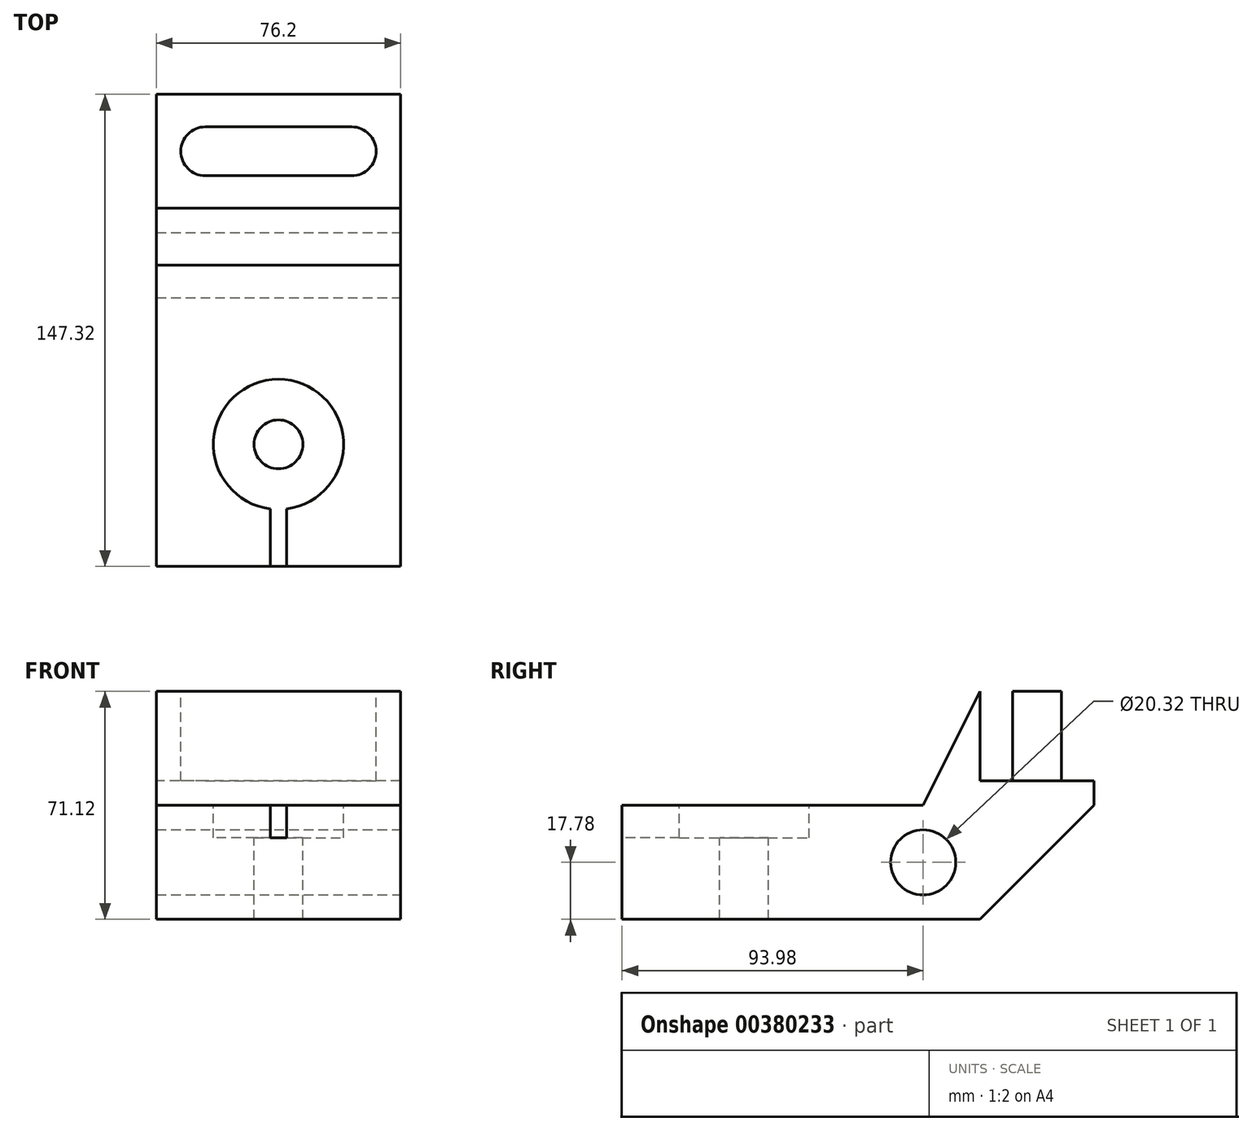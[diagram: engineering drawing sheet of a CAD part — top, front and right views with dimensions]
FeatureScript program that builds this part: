
annotation { "Feature Type Name" : "Feature", "Feature Type Description" : "" }
export const myFeature = defineFeature(function(context is Context, id is Id, definition is map)
    precondition{}
    {
        {
            var Q0;
            Q0=qCreatedBy(makeId("Right.planeOp"),FACE);
            var sketch = newSketch(context, id + "F0", { "sketchPlane" : qUnion([Q0])});
            skLineSegment(sketch, "E0.bottom", {"start": v(0, 0) * mm, "end": v(111.76, 0) * mm});
            skLineSegment(sketch, "E0.top", {"start": v(0, 35.56) * mm, "end": v(93.98, 35.56) * mm});
            skLineSegment(sketch, "E0.left", {"start": v(0, 0) * mm, "end": v(0, 35.56) * mm});
            skPoint(sketch, "E1", {"position": v(111.76, 0) * mm});
            skLineSegment(sketch, "E2", {"start": v(147.32, 35.56) * mm, "end": v(111.76, 0) * mm});
            skPoint(sketch, "E3", {"position": v(93.98, 35.56) * mm});
            skLineSegment(sketch, "E4", {"start": v(147.32, 35.56) * mm, "end": v(147.32, 71.12) * mm});
            skLineSegment(sketch, "E5", {"start": v(147.32, 71.12) * mm, "end": v(111.76, 71.12) * mm});
            skLineSegment(sketch, "E6", {"start": v(111.76, 71.12) * mm, "end": v(93.98, 35.56) * mm});
            skSolve(sketch);
        }
        {
            var Q0;
            Q0 = qSketchRegion(id + "F0", true);
            extrude(context, id + "F1", {"entities" : qUnion([Q0]), "depth" : 76.2 * mm});
        }
        {
            var Q0;
            Q0=makeQuery(id+"F1.opExtrude","CAP_FACE",FACE,{"disambiguationData":[OSD([sQuery(id+"F0.wireOp",EDGE,"E0.bottom"),sQuery(id+"F0.wireOp",EDGE,"E0.top"),sQuery(id+"F0.wireOp",EDGE,"E0.left"),sQuery(id+"F0.wireOp",EDGE,"E2"),sQuery(id+"F0.wireOp",EDGE,"E4"),sQuery(id+"F0.wireOp",EDGE,"E5"),sQuery(id+"F0.wireOp",EDGE,"E6")])],"isStart":false});
            var sketch = newSketch(context, id + "F2", { "sketchPlane" : qUnion([Q0])});
            skPoint(sketch, "E7", {"position": v(93.98, 17.78) * mm});
            skCircle(sketch, "E8", {"center": v(93.98, 17.78) * mm, "radius": 10.16 * mm});
            skSolve(sketch);
        }
        {
            var Q0;
            Q0 = qSketchRegion(id + "F2", true);
            var Q1;
            Q1=makeQuery(id+"F1.opExtrude","CAP_FACE",FACE,{"disambiguationData":[OSD([sQuery(id+"F0.wireOp",EDGE,"E0.bottom"),sQuery(id+"F0.wireOp",EDGE,"E0.top"),sQuery(id+"F0.wireOp",EDGE,"E0.left"),sQuery(id+"F0.wireOp",EDGE,"E2"),sQuery(id+"F0.wireOp",EDGE,"E4"),sQuery(id+"F0.wireOp",EDGE,"E5"),sQuery(id+"F0.wireOp",EDGE,"E6")])],"isStart":true});
            extrude(context, id + "F3", {"entities" : qUnion([Q0]), "operationType" : NewBodyOperationType.REMOVE, "endBound" : BoundingType.UP_TO_SURFACE, "oppositeDirection" : true, "endBoundEntityFace" : qUnion([Q1]), "depth" : 25.4 * mm});
        }
        {
            var Q0;
            Q0=makeQuery(id+"F1.opExtrude","SWEPT_FACE",FACE,{"disambiguationData":[OSD([sQuery(id+"F0.wireOp",EDGE,"E5")])]});
            var sketch = newSketch(context, id + "F4", { "sketchPlane" : qUnion([Q0])});
            skPoint(sketch, "E9.orphan", {"position": v(0, 129.54) * mm});
            skArc(sketch, "E10.0.startCap", {"start": v(15.24, 121.92) * mm, "mid": v(7.62, 129.54) * mm, "end": v(15.24, 137.16) * mm});
            skArc(sketch, "E10.0.endCap", {"start": v(60.96, 137.16) * mm, "mid": v(68.58, 129.54) * mm, "end": v(60.96, 121.92) * mm});
            skLineSegment(sketch, "E10.0.left", {"start": v(15.24, 137.16) * mm, "end": v(60.96, 137.16) * mm});
            skLineSegment(sketch, "E10.0.right", {"start": v(15.24, 121.92) * mm, "end": v(60.96, 121.92) * mm});
            skSolve(sketch);
        }
        {
            var Q0;
            Q0=makeQuery(id+"F4.imprint","IMPRINT",FACE,{"disambiguationData":[TD([[makeQuery(id+"F4.imprint","IMPRINT",EDGE,{"derivedFrom":sQuery(id+"F4.wireOp",EDGE,"E10.0.startCap")}),-1.0]])]});
            extrude(context, id + "F5", {"entities" : qUnion([Q0]), "operationType" : NewBodyOperationType.REMOVE, "oppositeDirection" : true, "depth" : 27.94 * mm});
        }
        {
            var Q0;
            Q0=makeQuery(id+"F1.opExtrude","SWEPT_FACE",FACE,{"disambiguationData":[OSD([sQuery(id+"F0.wireOp",EDGE,"E0.top")])]});
            var sketch = newSketch(context, id + "F6", { "sketchPlane" : qUnion([Q0])});
            skPoint(sketch, "E11", {"position": v(38.1, 38.1) * mm});
            skPoint(sketch, "E11.positionSnap0", {"position": v(38.1, 0) * mm});
            skSolve(sketch);
        }
        {
            var Q0;
            Q0=sQuery(id+"F6.wireOp",VERTEX,"E11");
            var Q1;
            Q1=makeQuery(id+"F1.opExtrude","SWEPT_BODY",BODY,{"disambiguationData":[OSD([sQuery(id+"F0.wireOp",EDGE,"E0.bottom"),sQuery(id+"F0.wireOp",EDGE,"E0.top"),sQuery(id+"F0.wireOp",EDGE,"E0.left"),sQuery(id+"F0.wireOp",EDGE,"E2"),sQuery(id+"F0.wireOp",EDGE,"E4"),sQuery(id+"F0.wireOp",EDGE,"E5"),sQuery(id+"F0.wireOp",EDGE,"E6")])]});
            hole(context, id + "F7", {"style" : HoleStyle.C_BORE, "endStyle" : HoleEndStyle.THROUGH, "holeDiameter" : 15.24 * mm, "cBoreDiameter" : 40.64 * mm, "cBoreDepth" : 10.16 * mm, "isTappedThrough" : true, "tappedDepth" : 12.7 * mm, "tapClearance" : 3, "locations" : qUnion([Q0]), "scope" : qUnion([Q1])});
        }
        {
            var Q0;
            Q0=makeQuery(id+"F1.opExtrude","SWEPT_FACE",FACE,{"disambiguationData":[OSD([sQuery(id+"F0.wireOp",EDGE,"E0.left")])]});
            var sketch = newSketch(context, id + "F8", { "sketchPlane" : qUnion([Q0])});
            skLineSegment(sketch, "E12.bottom", {"start": v(40.64, 25.4) * mm, "end": v(35.56, 25.4) * mm});
            skLineSegment(sketch, "E12.left", {"start": v(40.64, 25.4) * mm, "end": v(40.64, 35.56) * mm});
            skLineSegment(sketch, "E12.right", {"start": v(35.56, 25.4) * mm, "end": v(35.56, 35.56) * mm});
            skPoint(sketch, "E12.middle", {"position": v(38.1, 35.56) * mm});
            skPoint(sketch, "E13", {"position": v(35.56, 35.56) * mm});
            skPoint(sketch, "E14", {"position": v(40.64, 35.56) * mm});
            skSolve(sketch);
        }
        {
            var Q0;
            Q0=makeQuery(id+"F8.imprint","IMPRINT",FACE,{"disambiguationData":[TD([[makeQuery(id+"F8.imprint","IMPRINT",EDGE,{"derivedFrom":sQuery(id+"F8.wireOp",EDGE,"E12.bottom")}),-1.0]])]});
            extrude(context, id + "F9", {"entities" : qUnion([Q0]), "operationType" : NewBodyOperationType.REMOVE, "oppositeDirection" : true, "depth" : 19.05 * mm});
        }
    });
